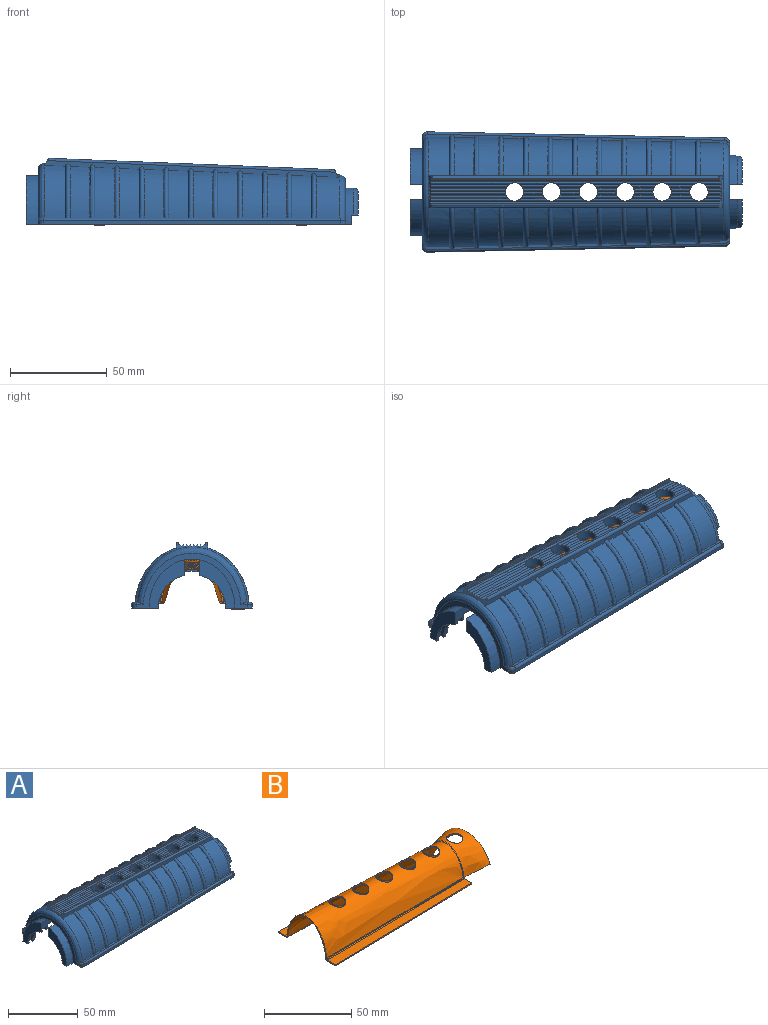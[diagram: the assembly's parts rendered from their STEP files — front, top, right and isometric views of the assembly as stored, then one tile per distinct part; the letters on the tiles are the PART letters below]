
ASSEMBLY  parts=2 mates=1
PART A: 246 faces, bbox 229.3x149.4x113.7 mm
  f0: cylinder r=17.46mm len=17.01mm, axis (1,0,0), area 29.8mm2, adj f13,f41,f198,f243
  f1: cylinder r=17.46mm len=17.01mm, axis (1,0,0), area 29.8mm2, adj f12,f137,f199,f242
  f2: cone r=3.81mm half-angle=3deg, axis (0,0,1), area 122.1mm2, adj f13,f15,f40,f204,f237,f238,f239
  f3: cone r=3.81mm half-angle=3deg, axis (0,0,1), area 132.4mm2, adj f13,f14,f15,f39,f234,f235,f236
  f4: cone r=3.81mm half-angle=3deg, axis (0,0,1), area 142.5mm2, adj f8,f13,f14,f205,f231,f232,f233
  f5: cone r=3.81mm half-angle=3deg, axis (0,0,1), area 142.5mm2, adj f8,f12,f14,f205,f228,f229,f230
  f6: cone r=3.81mm half-angle=3deg, axis (0,0,1), area 132.4mm2, adj f12,f14,f15,f38,f225,f226,f227
  f7: cone r=3.81mm half-angle=3deg, axis (0,0,1), area 122.1mm2, adj f12,f15,f40,f204,f222,f223,f224
  f8: offset ~81.13x59.72mm, area 2868.9mm2, adj f4,f5,f9,f10,f11,f12,f13,f199
  f9: plane 8.31x3.82mm, normal (1,0,0), area 24.3mm2, adj f8,f197,f199,f217
  f10: plane 28.95x23.02mm, normal (1,0,0), area 200.2mm2, adj f8,f12,f144,f199,f220,f221
  f11: plane 85.09x79.17mm, normal (1,0,0), area 200.2mm2, adj f8,f13,f44,f198,f215,f218
  f12: plane 224.2x69.53mm, normal (0,0,-1), area 994.6mm2, adj f1,f5,f6,f7,f8,f10,f14,f15
  f13: plane 226.06x71.39mm, normal (0,0,-1), area 994.6mm2, adj f0,f2,f3,f4,f8,f11,f14,f15
  f14: offset ~79.55x57.68mm, area 4950.3mm2, adj f3,f4,f5,f6,f12,f13,f38,f39
  f15: offset ~76.82x55.29mm, area 4608.6mm2, adj f2,f3,f6,f7,f12,f13,f38,f39
  f16: plane 150.68x7.49mm, normal (0.03,0.71,0.71), area 182mm2, adj f18,f19,f71,f72,f91,f101,f111,f159
  f17: plane 150.7x7.51mm, normal (0.03,-0.71,0.71), area 181.7mm2, adj f36,f37,f89,f90,f100,f110,f120,f159
  f18: plane 15.79x1.59mm, normal (0.03,-0.71,0.71), area 17.6mm2, adj f16,f21,f173,f206
  f19: plane 15.79x1.59mm, normal (0.03,-0.71,0.71), area 17.6mm2, adj f16,f20,f174,f206
  f20: plane 12.78x1.42mm, normal (0.03,0.71,0.71), area 14.9mm2, adj f19,f23,f174,f206
  f21: plane 12.78x1.42mm, normal (0.03,0.71,0.71), area 14.9mm2, adj f18,f22,f173,f206
  f22: plane 11.19x1.34mm, normal (0.03,-0.71,0.71), area 13.4mm2, adj f21,f25,f173,f206
  f23: plane 11.19x1.34mm, normal (0.03,-0.71,0.71), area 13.4mm2, adj f20,f24,f174,f206
  f24: plane 10.23x1.3mm, normal (0.03,0.71,0.71), area 12.5mm2, adj f23,f27,f174,f206
  f25: plane 10.23x1.3mm, normal (0.03,0.71,0.71), area 12.5mm2, adj f22,f26,f173,f206
  f26: plane 9.7x1.28mm, normal (0.03,-0.71,0.71), area 12.1mm2, adj f25,f29,f173,f206
  f27: plane 9.7x1.28mm, normal (0.03,-0.71,0.71), area 12.1mm2, adj f24,f28,f174,f206
  f28: plane 9.7x1.28mm, normal (0.03,0.71,0.71), area 12mm2, adj f27,f31,f174,f206
  f29: plane 9.7x1.28mm, normal (0.03,0.71,0.71), area 12mm2, adj f26,f30,f173,f206
  f30: plane 10.22x1.3mm, normal (0.03,-0.71,0.71), area 12.5mm2, adj f29,f33,f173,f206
  f31: plane 10.22x1.3mm, normal (0.03,-0.71,0.71), area 12.5mm2, adj f28,f32,f174,f206
  f32: plane 11.18x1.34mm, normal (0.03,0.71,0.71), area 13.4mm2, adj f31,f35,f174,f206
  f33: plane 11.18x1.34mm, normal (0.03,0.71,0.71), area 13.4mm2, adj f30,f34,f173,f206
  f34: plane 12.75x1.42mm, normal (0.03,-0.71,0.71), area 14.9mm2, adj f33,f37,f173,f206
  f35: plane 12.75x1.42mm, normal (0.03,-0.71,0.71), area 14.9mm2, adj f32,f36,f174,f206
  f36: plane 15.74x1.59mm, normal (0.03,0.71,0.71), area 17.6mm2, adj f17,f35,f174,f206
  f37: plane 15.74x1.59mm, normal (0.03,0.71,0.71), area 17.6mm2, adj f17,f34,f173,f206
  f38: bspline ~21.22x16.17mm, area 99.1mm2, adj f6,f14,f15,f206
  f39: bspline ~22.14x18.27mm, area 99.1mm2, adj f3,f14,f15,f206
  f40: offset ~74.08x50.66mm, area 1618.4mm2, adj f2,f7,f12,f13,f145,f171,f204
  f41: plane 25.12x18.33mm, normal (-1,0,0), area 172.2mm2, adj f0,f13,f42,f198
  f42: extruded ~24.99x18.26mm, area 212.3mm2, adj f13,f41,f139,f198
  f43: cylinder r=17.46mm len=17.01mm, axis (1,0,0), area 29.8mm2, adj f13,f45,f198,f244
  f44: extruded ~21.73x15.08mm, area 90.3mm2, adj f11,f13,f45,f198
  f45: plane 21.77x15.1mm, normal (1,0,0), area 73.9mm2, adj f13,f43,f44,f198
  f46: cylinder r=19.05mm len=18.63mm, axis (-1,0,0), area 104.4mm2, adj f12,f48,f140,f194,f200,f201
  f47: cylinder r=17.46mm len=17.01mm, axis (1,0,0), area 207.8mm2, adj f12,f48,f145,f194,f200,f201
  f48: torus R=16.83mm, axis (1,0,0), area 57.2mm2, adj f46,f47,f194,f201
  f49: bspline ~158.75x48.38mm, area 298.7mm2, adj f69,f70,f161,f183
  f50: bspline ~158.75x48.89mm, area 304.9mm2, adj f68,f69,f161,f183
  f51: bspline ~158.75x48.89mm, area 311mm2, adj f67,f68,f161,f183
  f52: bspline ~158.75x48.89mm, area 317.1mm2, adj f66,f67,f161,f183
  f53: bspline ~158.75x48.89mm, area 323.2mm2, adj f65,f66,f161,f183
  f54: bspline ~158.75x48.89mm, area 329.3mm2, adj f64,f65,f161,f183
  f55: bspline ~158.75x48.89mm, area 335.4mm2, adj f63,f64,f161,f183
  f56: bspline ~158.75x48.89mm, area 341.6mm2, adj f62,f63,f161,f183
  f57: bspline ~158.75x48.89mm, area 347.7mm2, adj f61,f62,f161,f183
  f58: bspline ~158.75x48.89mm, area 353.8mm2, adj f60,f61,f161,f183
  f59: bspline ~158.75x48.89mm, area 379.3mm2, adj f60,f123,f161,f183
  f60: bspline ~27.95x21.53mm, area 144.9mm2, adj f58,f59,f161,f183
  f61: bspline ~27.44x21.27mm, area 142.5mm2, adj f57,f58,f161,f183
  f62: bspline ~26.93x21.02mm, area 140.1mm2, adj f56,f57,f161,f183
  f63: bspline ~26.42x20.76mm, area 137.6mm2, adj f55,f56,f161,f183
  f64: bspline ~25.91x20.5mm, area 135.2mm2, adj f54,f55,f161,f183
  f65: bspline ~25.4x20.24mm, area 132.8mm2, adj f53,f54,f161,f183
  f66: bspline ~24.89x19.99mm, area 130.4mm2, adj f52,f53,f161,f183
  f67: bspline ~24.38x19.73mm, area 128mm2, adj f51,f52,f161,f183
  f68: bspline ~23.88x19.47mm, area 125.6mm2, adj f50,f51,f161,f183
  f69: bspline ~23.5x19.23mm, area 123.6mm2, adj f49,f50,f161,f183
  f70: bspline ~23x18.97mm, area 121.2mm2, adj f49,f125,f161,f183
  f71: plane 15.79x1.59mm, normal (0.03,-0.71,0.71), area 17.6mm2, adj f16,f74,f174,f175
  f72: plane 41.96x2.62mm, normal (0.03,-0.71,0.71), area 51.2mm2, adj f16,f73,f160,f175
  f73: plane 40.41x2.53mm, normal (0.03,0.71,0.71), area 49.9mm2, adj f72,f76,f160,f175
  f74: plane 12.78x1.42mm, normal (0.03,0.71,0.71), area 14.9mm2, adj f71,f75,f174,f175
  f75: plane 11.19x1.34mm, normal (0.03,-0.71,0.71), area 13.4mm2, adj f74,f78,f174,f175
  f76: plane 39.61x2.46mm, normal (0.03,-0.71,0.71), area 49.1mm2, adj f73,f77,f160,f175
  f77: plane 39.12x2.44mm, normal (0.03,0.71,0.71), area 48.7mm2, adj f76,f80,f160,f175
  f78: plane 10.23x1.3mm, normal (0.03,0.71,0.71), area 12.5mm2, adj f75,f79,f174,f175
  f79: plane 9.7x1.28mm, normal (0.03,-0.71,0.71), area 12.1mm2, adj f78,f82,f174,f175
  f80: plane 38.85x2.42mm, normal (0.03,-0.71,0.71), area 48.4mm2, adj f77,f81,f160,f175
  f81: plane 38.85x2.42mm, normal (0.03,0.71,0.71), area 48.4mm2, adj f80,f84,f160,f175
  f82: plane 9.7x1.28mm, normal (0.03,0.71,0.71), area 12mm2, adj f79,f83,f174,f175
  f83: plane 10.22x1.3mm, normal (0.03,-0.71,0.71), area 12.5mm2, adj f82,f86,f174,f175
  f84: plane 39.11x2.44mm, normal (0.03,-0.71,0.71), area 48.7mm2, adj f81,f85,f160,f175
  f85: plane 39.6x2.46mm, normal (0.03,0.71,0.71), area 49.1mm2, adj f84,f88,f160,f175
  f86: plane 11.18x1.34mm, normal (0.03,0.71,0.71), area 13.4mm2, adj f83,f87,f174,f175
  f87: plane 12.75x1.42mm, normal (0.03,-0.71,0.71), area 14.9mm2, adj f86,f90,f174,f175
  f88: plane 40.4x2.53mm, normal (0.03,-0.71,0.71), area 49.9mm2, adj f85,f89,f160,f175
  f89: plane 41.93x2.61mm, normal (0.03,0.71,0.71), area 51.2mm2, adj f17,f88,f160,f175
  f90: plane 15.74x1.59mm, normal (0.03,0.71,0.71), area 17.6mm2, adj f17,f87,f174,f175
  f91: plane 15.79x1.59mm, normal (0.03,-0.71,0.71), area 17.6mm2, adj f16,f92,f172,f173
  f92: plane 12.78x1.42mm, normal (0.03,0.71,0.71), area 14.9mm2, adj f91,f93,f172,f173
  f93: plane 11.19x1.34mm, normal (0.03,-0.71,0.71), area 13.4mm2, adj f92,f94,f172,f173
  f94: plane 10.23x1.3mm, normal (0.03,0.71,0.71), area 12.5mm2, adj f93,f95,f172,f173
  f95: plane 9.7x1.28mm, normal (0.03,-0.71,0.71), area 12.1mm2, adj f94,f96,f172,f173
  f96: plane 9.7x1.28mm, normal (0.03,0.71,0.71), area 12mm2, adj f95,f97,f172,f173
  f97: plane 10.22x1.3mm, normal (0.03,-0.71,0.71), area 12.5mm2, adj f96,f98,f172,f173
  f98: plane 11.18x1.34mm, normal (0.03,0.71,0.71), area 13.4mm2, adj f97,f99,f172,f173
  f99: plane 12.75x1.42mm, normal (0.03,-0.71,0.71), area 14.9mm2, adj f98,f100,f172,f173
  f100: plane 15.74x1.59mm, normal (0.03,0.71,0.71), area 17.6mm2, adj f17,f99,f172,f173
  f101: plane 15.79x1.59mm, normal (0.03,-0.71,0.71), area 17.6mm2, adj f16,f102,f171,f172
  f102: plane 12.78x1.42mm, normal (0.03,0.71,0.71), area 14.9mm2, adj f101,f103,f171,f172
  f103: plane 11.19x1.34mm, normal (0.03,-0.71,0.71), area 13.4mm2, adj f102,f104,f171,f172
  f104: plane 10.23x1.3mm, normal (0.03,0.71,0.71), area 12.5mm2, adj f103,f105,f171,f172
  f105: plane 9.7x1.28mm, normal (0.03,-0.71,0.71), area 12.1mm2, adj f104,f106,f171,f172
  f106: plane 9.7x1.28mm, normal (0.03,0.71,0.71), area 12mm2, adj f105,f107,f171,f172
  f107: plane 10.22x1.3mm, normal (0.03,-0.71,0.71), area 12.5mm2, adj f106,f108,f171,f172
  f108: plane 11.18x1.34mm, normal (0.03,0.71,0.71), area 13.4mm2, adj f107,f109,f171,f172
  f109: plane 12.75x1.42mm, normal (0.03,-0.71,0.71), area 14.9mm2, adj f108,f110,f171,f172
  f110: plane 15.74x1.59mm, normal (0.03,0.71,0.71), area 17.6mm2, adj f17,f109,f171,f172
  f111: plane 9.71x1.4mm, normal (0.03,-0.71,0.71), area 10.7mm2, adj f16,f112,f159,f171
  f112: plane 8.17x1.23mm, normal (0.03,0.71,0.71), area 9.4mm2, adj f111,f113,f159,f171
  f113: plane 7.36x1.21mm, normal (0.03,-0.71,0.71), area 8.6mm2, adj f112,f114,f159,f171
  f114: plane 6.88x1.17mm, normal (0.03,0.71,0.71), area 8.1mm2, adj f113,f115,f159,f171
  f115: plane 6.6x1.16mm, normal (0.03,-0.71,0.71), area 7.9mm2, adj f114,f116,f159,f171
  f116: plane 6.6x1.16mm, normal (0.03,0.71,0.71), area 7.9mm2, adj f115,f117,f159,f171
  f117: plane 6.87x1.17mm, normal (0.03,-0.71,0.71), area 8.1mm2, adj f116,f118,f159,f171
  f118: plane 7.35x1.21mm, normal (0.03,0.71,0.71), area 8.6mm2, adj f117,f119,f159,f171
  f119: plane 8.16x1.23mm, normal (0.03,-0.71,0.71), area 9.4mm2, adj f118,f120,f159,f171
  f120: plane 9.68x1.4mm, normal (0.03,0.71,0.71), area 10.7mm2, adj f17,f119,f159,f171
  f121: plane 147.56x5.9mm, normal (0.04,0,1), area 1.5mm2, adj f159,f160,f166,f170
  f122: bspline ~13.71x0.92mm, area 0mm2, adj f123,f160
  f123: bspline ~56.9x29.7mm, area 432.6mm2, adj f59,f122,f135,f139,f160,f161,f162,f179
  f124: bspline ~158.75x48.38mm, area 298.7mm2, adj f157,f158,f162,f179
  f125: bspline ~51.03x22.88mm, area 706.8mm2, adj f70,f141,f158,f159,f161,f162,f179,f183
  f126: bspline ~158.75x48.89mm, area 304.9mm2, adj f156,f157,f162,f179
  f127: bspline ~158.75x48.89mm, area 311mm2, adj f155,f156,f162,f179
  f128: bspline ~158.75x48.89mm, area 317.1mm2, adj f154,f155,f162,f179
  f129: bspline ~158.75x48.89mm, area 323.2mm2, adj f153,f154,f162,f179
  f130: bspline ~158.75x48.89mm, area 329.3mm2, adj f152,f153,f162,f179
  f131: bspline ~158.75x48.89mm, area 335.4mm2, adj f151,f152,f162,f179
  f132: bspline ~158.75x48.89mm, area 341.6mm2, adj f150,f151,f162,f179
  f133: bspline ~158.75x48.89mm, area 347.7mm2, adj f149,f150,f162,f179
  f134: bspline ~158.75x48.89mm, area 353.8mm2, adj f148,f149,f162,f179
  f135: bspline ~158.75x48.89mm, area 379.3mm2, adj f123,f148,f162,f179
  f136: cylinder r=19.05mm len=18.63mm, axis (-1,0,0), area 104.4mm2, adj f13,f140,f147,f195,f202,f203
  f137: plane 25.12x18.34mm, normal (-1,0,0), area 172mm2, adj f1,f12,f138,f199
  f138: extruded ~24.99x18.26mm, area 212.3mm2, adj f12,f137,f139,f199
  f139: plane 57.08x28.48mm, normal (-1,0,0), area 258.6mm2, adj f12,f13,f42,f123,f138,f178,f180,f184
  f140: plane 50.9x22.35mm, normal (1,0,0), area 224.7mm2, adj f12,f13,f46,f136,f141,f176,f182,f188
  f141: bspline ~50.92x26.25mm, area 345.2mm2, adj f125,f140,f179,f183,f188,f193
  f142: cylinder r=17.46mm len=17.01mm, axis (1,0,0), area 29.8mm2, adj f12,f146,f199,f241
  f143: cylinder r=17.46mm len=17.01mm, axis (1,0,0), area 207.8mm2, adj f13,f145,f147,f195,f202,f203
  f144: extruded ~21.73x15.08mm, area 90.3mm2, adj f10,f12,f146,f199
  f145: plane 93.65x71.43mm, normal (-1,0,0), area 290.8mm2, adj f12,f13,f40,f47,f143,f194,f195,f196
  f146: plane 21.77x15.1mm, normal (1,0,0), area 73.9mm2, adj f12,f142,f144,f199
  f147: torus R=16.83mm, axis (1,0,0), area 57.2mm2, adj f136,f143,f195,f202
  f148: bspline ~27.95x21.53mm, area 144.9mm2, adj f134,f135,f162,f179
  f149: bspline ~27.44x21.27mm, area 142.5mm2, adj f133,f134,f162,f179
  f150: bspline ~26.93x21.02mm, area 140.1mm2, adj f132,f133,f162,f179
  f151: bspline ~26.42x20.76mm, area 137.6mm2, adj f131,f132,f162,f179
  f152: bspline ~25.91x20.5mm, area 135.2mm2, adj f130,f131,f162,f179
  f153: bspline ~25.4x20.24mm, area 132.8mm2, adj f129,f130,f162,f179
  f154: bspline ~24.89x19.99mm, area 130.4mm2, adj f128,f129,f162,f179
  f155: bspline ~24.38x19.73mm, area 128mm2, adj f127,f128,f162,f179
  f156: bspline ~23.88x19.47mm, area 125.6mm2, adj f126,f127,f162,f179
  f157: bspline ~23.5x19.23mm, area 123.6mm2, adj f124,f126,f162,f179
  f158: bspline ~23x18.97mm, area 121.2mm2, adj f124,f125,f162,f179
  f159: plane 17.98x5.47mm, normal (0.89,0,0.46), area 29.4mm2, adj f16,f17,f111,f112,f113,f114,f115,f116
  f160: plane 17.65x4.94mm, normal (-0.85,0,0.53), area 29.3mm2, adj f16,f17,f72,f73,f76,f77,f80,f81
  f161: plane 152.07x8.66mm, normal (0,-1,0), area 367.3mm2, adj f49,f50,f51,f52,f53,f54,f55,f56
  f162: plane 152.07x8.66mm, normal (0,1,0), area 367.3mm2, adj f123,f124,f125,f126,f127,f128,f129,f130
  f163: plane 150.05x6.87mm, normal (0.03,-0.71,0.71), area 188.1mm2, adj f16,f159,f160,f168
  f164: plane 150.05x6.87mm, normal (0.03,0.71,0.71), area 188.1mm2, adj f17,f159,f160,f165
  f165: plane 149.03x5.96mm, normal (0.04,0,1), area 112.9mm2, adj f159,f160,f164,f166
  f166: plane 149.03x7.2mm, normal (0,1,0), area 188.3mm2, adj f121,f159,f160,f165
  f167: plane 149.03x7.2mm, normal (0,-1,0), area 188.3mm2, adj f159,f160,f168,f169
  f168: plane 149.03x5.96mm, normal (0.04,0,1), area 112.9mm2, adj f159,f160,f163,f167
  f169: cylinder r=1.27mm len=149.08mm, axis (-1,0,0.04), area 296.1mm2, adj f159,f160,f162,f167
  f170: cylinder r=1.27mm len=149.08mm, axis (1,0,-0.04), area 296.1mm2, adj f121,f159,f160,f161
  f171: cylinder r=4.76mm len=9.53mm, axis (0,0,-1), area 127.8mm2, adj f16,f17,f40,f101,f102,f103,f104,f105
  f172: cylinder r=4.76mm len=9.53mm, axis (0,0,-1), area 125.7mm2, adj f15,f16,f17,f91,f92,f93,f94,f95
  f173: cylinder r=4.76mm len=9.53mm, axis (0,0,-1), area 127.8mm2, adj f15,f16,f17,f18,f21,f22,f25,f26
  f174: cylinder r=4.76mm len=9.53mm, axis (0,0,-1), area 125.7mm2, adj f14,f16,f17,f19,f20,f23,f24,f27
  f175: cylinder r=4.76mm len=9.53mm, axis (0,0,-1), area 125.7mm2, adj f14,f16,f17,f71,f72,f73,f74,f75
  f176: cylinder r=2.54mm len=2.54mm, axis (0,0,-1), area 7.5mm2, adj f12,f140,f177,f187
  f177: plane 153.67x3.07mm, normal (0.02,1,0), area 292.8mm2, adj f12,f176,f178,f186
  f178: cylinder r=2.54mm len=2.59mm, axis (0,0,-1), area 7.7mm2, adj f12,f139,f177,f185
  f179: plane 156.65x5.61mm, normal (0,0,1), area 196.5mm2, adj f123,f124,f125,f126,f127,f128,f129,f130
  f180: cylinder r=2.54mm len=2.59mm, axis (0,0,-1), area 7.7mm2, adj f13,f139,f181,f190
  f181: plane 153.67x3.07mm, normal (0.02,-1,0), area 292.8mm2, adj f13,f180,f182,f191
  f182: cylinder r=2.54mm len=2.54mm, axis (0,0,-1), area 7.5mm2, adj f13,f140,f181,f192
  f183: plane 156.65x5.61mm, normal (0,0,1), area 196.5mm2, adj f49,f50,f51,f52,f53,f54,f55,f56
  f184: cylinder r=1.27mm len=3.24mm, axis (0,1,0), area 4mm2, adj f123,f139,f179,f185
  f185: torus R=1.27mm, axis (0,0,1), area 6.6mm2, adj f178,f179,f184,f186
  f186: cylinder r=1.27mm len=153.7mm, axis (1,-0.02,0), area 306.6mm2, adj f177,f179,f185,f187
  f187: torus R=1.27mm, axis (0,0,1), area 6.4mm2, adj f176,f179,f186,f188
  f188: cylinder r=1.27mm len=3.24mm, axis (0,1,0), area 4.1mm2, adj f140,f141,f179,f187
  f189: cylinder r=1.27mm len=3.24mm, axis (0,-1,0), area 4mm2, adj f123,f139,f183,f190
  f190: torus R=1.27mm, axis (0,0,1), area 6.6mm2, adj f180,f183,f189,f191
  f191: cylinder r=1.27mm len=153.7mm, axis (-1,-0.02,0), area 306.6mm2, adj f181,f183,f190,f192
  f192: torus R=1.27mm, axis (0,0,1), area 6.4mm2, adj f182,f183,f191,f193
  f193: cylinder r=1.27mm len=3.24mm, axis (0,-1,0), area 4.1mm2, adj f140,f141,f183,f192
  f194: plane 9.7x1.8mm, normal (0,-1,0), area 14.6mm2, adj f46,f47,f48,f145,f196
  f195: plane 9.7x1.8mm, normal (0,1,0), area 14.6mm2, adj f136,f143,f145,f147,f196
  f196: cylinder r=19.05mm len=7.94mm, axis (-1,0,0), area 25.4mm2, adj f140,f145,f194,f195
  f197: extruded ~7.94x3.18mm, area 25.4mm2, adj f9,f139,f198,f199
  f198: plane 9.53x7.98mm, normal (0,1,0), area 52.4mm2, adj f0,f11,f41,f42,f43,f44,f45,f197
  f199: plane 22.23x11.09mm, normal (0,-1,0), area 88.6mm2, adj f1,f8,f9,f10,f137,f138,f142,f144
  f200: plane 4.76x2.25mm, normal (1,0,0), area 7.6mm2, adj f12,f46,f47,f201
  f201: plane 3.38x1.85mm, normal (0,0,-1), area 4.3mm2, adj f46,f47,f48,f200
  f202: plane 3.38x1.86mm, normal (0,0,-1), area 4.3mm2, adj f136,f143,f147,f203
  f203: plane 4.76x2.25mm, normal (1,0,0), area 7.6mm2, adj f13,f136,f143,f202
  f204: bspline ~43.88x15.67mm, area 220.8mm2, adj f2,f7,f15,f40
  f205: bspline ~47.58x17.94mm, area 252.5mm2, adj f4,f5,f8,f14
  f206: cylinder r=4.76mm len=9.53mm, axis (0,0,-1), area 142.2mm2, adj f14,f15,f16,f17,f18,f19,f20,f21
  f207: cylinder r=2.54mm len=5.08mm, axis (0,0,1), area 12.7mm2, adj f13,f208
  f208: plane 5.08x5.08mm, normal (0,0,-1), area 20.3mm2, adj f207
  f209: cylinder r=2.54mm len=5.08mm, axis (0,0,1), area 12.7mm2, adj f13,f210
  f210: plane 5.08x5.08mm, normal (0,0,-1), area 20.3mm2, adj f209
  f211: cylinder r=2.54mm len=5.08mm, axis (0,0,-1), area 12.7mm2, adj f12,f212
  f212: plane 5.08x5.08mm, normal (0,0,-1), area 20.3mm2, adj f211
  f213: cylinder r=2.54mm len=5.08mm, axis (0,0,-1), area 12.7mm2, adj f12,f214
  f214: plane 5.08x5.08mm, normal (0,0,-1), area 20.3mm2, adj f213
  f215: plane 13.89x3.49mm, normal (0,-1,0), area 26mm2, adj f8,f11,f216,f218
  f216: cylinder r=1.59mm len=3.18mm, axis (0,0,-1), area 11mm2, adj f8,f215,f217,f218
  f217: plane 13.04x3.45mm, normal (0,1,0), area 36.2mm2, adj f8,f9,f216,f218
  f218: plane 14.29x3.18mm, normal (0,0,-1), area 44.3mm2, adj f11,f215,f216,f217
  f219: cylinder r=1.59mm len=3.18mm, axis (0,0,-1), area 11mm2, adj f8,f199,f220,f221
  f220: plane 12.7x2.31mm, normal (0,1,0), area 26mm2, adj f8,f10,f219,f221
  f221: plane 14.29x3.18mm, normal (0,0,-1), area 44.3mm2, adj f10,f199,f219,f220
  f222: plane 7.22x2.43mm, normal (0,0,1), area 12.3mm2, adj f7,f224
  f223: plane 7.31x2.47mm, normal (0,0,-1), area 12.6mm2, adj f7,f224
  f224: plane 7.31x0.79mm, normal (-0.02,-1,0), area 5.8mm2, adj f7,f222,f223
  f225: plane 7.22x2.43mm, normal (0,0,1), area 12.3mm2, adj f6,f227
  f226: plane 7.31x2.47mm, normal (0,0,-1), area 12.6mm2, adj f6,f227
  f227: plane 7.31x0.79mm, normal (-0.02,-1,0), area 5.8mm2, adj f6,f225,f226
  f228: plane 7.22x2.43mm, normal (0,0,1), area 12.3mm2, adj f5,f230
  f229: plane 7.31x2.47mm, normal (0,0,-1), area 12.6mm2, adj f5,f230
  f230: plane 7.31x0.79mm, normal (-0.02,-1,0), area 5.8mm2, adj f5,f228,f229
  f231: plane 7.22x2.43mm, normal (0,0,1), area 12.3mm2, adj f4,f233
  f232: plane 7.31x2.47mm, normal (0,0,-1), area 12.6mm2, adj f4,f233
  f233: plane 7.31x0.79mm, normal (-0.02,1,0), area 5.8mm2, adj f4,f231,f232
  f234: plane 7.22x2.43mm, normal (0,0,1), area 12.3mm2, adj f3,f236
  f235: plane 7.31x2.47mm, normal (0,0,-1), area 12.6mm2, adj f3,f236
  f236: plane 7.31x0.79mm, normal (-0.02,1,0), area 5.8mm2, adj f3,f234,f235
  f237: plane 7.31x0.79mm, normal (-0.02,1,0), area 5.8mm2, adj f2,f238,f239
  f238: plane 7.31x2.47mm, normal (0,0,-1), area 12.6mm2, adj f2,f237
  f239: plane 7.22x2.43mm, normal (0,0,1), area 12.3mm2, adj f2,f237
  f240: cylinder r=19.69mm len=19.28mm, axis (1,0,0), area 102.6mm2, adj f12,f199,f241,f242
  f241: plane 19.28x15.72mm, normal (-1,0,0), area 56mm2, adj f12,f142,f199,f240
  f242: plane 19.28x15.72mm, normal (1,0,0), area 56mm2, adj f1,f12,f199,f240
  f243: plane 19.28x15.72mm, normal (1,0,0), area 56mm2, adj f0,f13,f198,f245
  f244: plane 19.28x15.72mm, normal (-1,0,0), area 56mm2, adj f13,f43,f198,f245
  f245: cylinder r=19.69mm len=19.28mm, axis (1,0,0), area 102.6mm2, adj f13,f198,f243,f244
PART B: 31 faces, bbox 177.5x65.5x54.2 mm
  f0: bspline ~152.4x63.95mm, area 5551mm2, adj f2,f15,f23,f24,f26,f27,f28,f29
  f1: offset ~39.16x18.48mm, area 778.8mm2, adj f7,f8,f9,f25
  f2: bspline ~37.57x16.92mm, area 743.3mm2, adj f0,f7,f8,f9,f25
  f3: plane 6.64x0.79mm, normal (-1,0,0), area 5.3mm2, adj f4,f16,f18,f22
  f4: plane 113.03x2.26mm, normal (0.02,-1,0), area 89.7mm2, adj f3,f5,f18,f22
  f5: plane 5.85x0.79mm, normal (1,0,0), area 4.6mm2, adj f4,f6,f18,f22
  f6: bspline ~1.26x1.21mm, area 1mm2, adj f5,f7,f20,f24
  f7: bspline ~16.51x5.3mm, area 14.1mm2, adj f1,f2,f6,f8
  f8: plane 39.09x15.21mm, normal (1,0,0), area 40.2mm2, adj f1,f2,f7,f9
  f9: bspline ~16.51x5.82mm, area 14mm2, adj f1,f2,f8,f10
  f10: bspline ~1.26x1.21mm, area 1mm2, adj f9,f11,f19,f23
  f11: plane 5.84x0.79mm, normal (1,0,0), area 4.6mm2, adj f10,f12,f17,f21
  f12: plane 113.03x2.26mm, normal (0.02,1,0), area 89.7mm2, adj f11,f13,f17,f21
  f13: plane 6.63x0.79mm, normal (-1,0,0), area 5.3mm2, adj f12,f14,f17,f21
  f14: bspline ~1.26x1.23mm, area 1mm2, adj f13,f15,f19,f23
  f15: bspline ~32.49x21.92mm, area 46.1mm2, adj f0,f14,f16
  f16: bspline ~1.26x1.23mm, area 1mm2, adj f3,f15,f20,f24
  f17: plane 113.03x8.1mm, normal (0,0,1), area 704.9mm2, adj f11,f12,f13,f19
  f18: plane 113.03x8.11mm, normal (0,0,1), area 705.5mm2, adj f3,f4,f5,f20
  f19: bspline ~156.83x2.51mm, area 78.8mm2, adj f10,f14,f17
  f20: bspline ~156.83x2.51mm, area 78.7mm2, adj f6,f16,f18
  f21: plane 113.03x8.1mm, normal (0,0,-1), area 704.9mm2, adj f11,f12,f13,f23
  f22: plane 113.03x8.11mm, normal (0,0,-1), area 705.5mm2, adj f3,f4,f5,f24
  f23: bspline ~156.84x3.3mm, area 210.1mm2, adj f0,f10,f14,f21
  f24: bspline ~156.84x3.3mm, area 209.9mm2, adj f0,f6,f16,f22
  f25: cylinder r=4.76mm len=9.53mm, axis (0,0,-1), area 24.6mm2, adj f1,f2
  f26: cylinder r=4.76mm len=9.53mm, axis (0,0,-1), area 25.1mm2, adj f0
  f27: cylinder r=4.76mm len=9.53mm, axis (0,0,-1), area 25.1mm2, adj f0
  f28: cylinder r=4.76mm len=9.53mm, axis (0,0,-1), area 25.1mm2, adj f0
  f29: cylinder r=4.76mm len=9.53mm, axis (0,0,-1), area 25.1mm2, adj f0
  f30: cylinder r=4.76mm len=9.53mm, axis (0,0,-1), area 25.1mm2, adj f0
PLACE A at identity fixed
PLACE B t=(0,0,0.02)mm
MATE fastened A.f171 <-> B.f25  axis (0,0,-1) through (-225.42,0,24.91)mm
